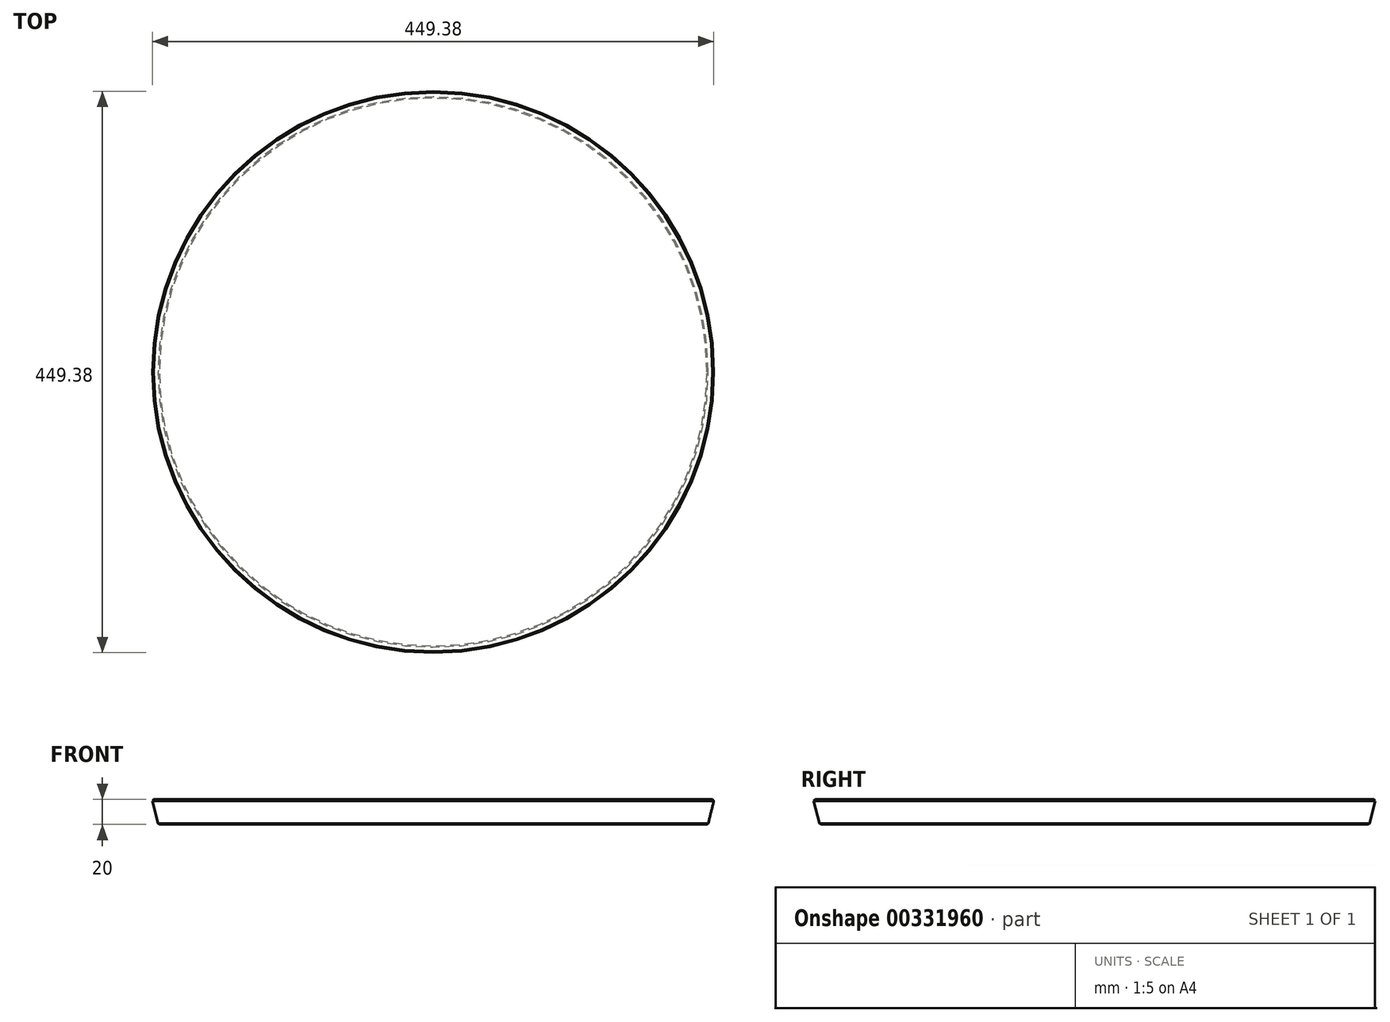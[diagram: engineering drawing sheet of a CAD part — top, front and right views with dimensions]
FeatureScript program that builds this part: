
annotation { "Feature Type Name" : "Feature", "Feature Type Description" : "" }
export const myFeature = defineFeature(function(context is Context, id is Id, definition is map)
    precondition{}
    {
        {
            var Q0;
            Q0=qCreatedBy(makeId("Top.planeOp"),FACE);
            var sketch = newSketch(context, id + "F0", { "sketchPlane" : qUnion([Q0])});
            skCircle(sketch, "E0", {"center": v(0, 0) * mm, "radius": 225 * mm});
            skSolve(sketch);
        }
        {
            var Q0;
            Q0 = qSketchRegion(id + "F0", true);
            extrude(context, id + "F1", {"entities" : qUnion([Q0]), "depth" : 20 * mm});
        }
        {
            var Q0;
            Q0=makeQuery(id+"F1.opExtrude","CAP_EDGE",EDGE,{"disambiguationData":[OSD([sQuery(id+"F0.wireOp",EDGE,"E0")])],"isStart":true});
            chamfer(context, id + "F2", {"entities" : qUnion([Q0]), "chamferType" : ChamferType.TWO_OFFSETS, "width1" : 20 * mm, "oppositeDirection" : false, "width2" : 5 * mm, "tangentPropagation" : true});
        }
        {
            var Q0;
            {var subQ0=sQuery(id+"F0.wireOp",EDGE,"E0");Q0=makeQuery(id+"F2.opChamfer","BLEND_EDGE",EDGE,{"blendedFrom":[makeQuery(id+"F1.opExtrude","CAP_EDGE",EDGE,{"disambiguationData":[OSD([subQ0])],"isStart":true}),makeQuery(id+"F1.opExtrude","CAP_FACE",FACE,{"disambiguationData":[OSD([subQ0])],"isStart":false})],"blendedInto":[makeQuery(id+"F1.opExtrude","CAP_FACE",FACE,{"disambiguationData":[OSD([subQ0])],"isStart":false})]});}
            chamfer(context, id + "F3", {"entities" : qUnion([Q0]), "width" : 1 * mm, "tangentPropagation" : true});
        }
        {
            var Q0;
            {var subQ0=sQuery(id+"F0.wireOp",EDGE,"E0");Q0=makeQuery(id+"F2.opChamfer","BLEND_EDGE",EDGE,{"blendedFrom":[makeQuery(id+"F1.opExtrude","CAP_EDGE",EDGE,{"disambiguationData":[OSD([subQ0])],"isStart":true}),makeQuery(id+"F1.opExtrude","CAP_FACE",FACE,{"disambiguationData":[OSD([subQ0])],"isStart":true})],"blendedInto":[makeQuery(id+"F1.opExtrude","CAP_FACE",FACE,{"disambiguationData":[OSD([subQ0])],"isStart":true})]});}
            chamfer(context, id + "F4", {"entities" : qUnion([Q0]), "width" : 1 * mm, "tangentPropagation" : true});
        }
    });
